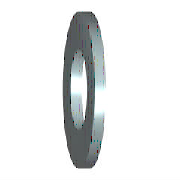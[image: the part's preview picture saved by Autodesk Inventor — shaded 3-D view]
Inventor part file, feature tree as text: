
AUTODESK INVENTOR PART (.ipt)
format: ipt  version: 2019.2 (Build 232265000, 265)  size: 106,496 bytes
history: native  units: mm (DEFAULTED — no unit token found)
features: other x1, plane x1, sketch x1
ambient origin geometry x7: Origin, YZ Plane, XY Plane, X Axis, Y Axis, Z Axis, Center Point
bodies: Solid1 (feature_tree), Body (feature_tree)
feature tree (3):
  other  "Work Axis1"
  plane  "Work Plane1"
  sketch  "Sketch"  dims[d0=10.5mm d1=18.0mm d2=1.6mm d3=0.0mm d4=0.0mm d5=0.0mm d6=0.0mm d7=0.0mm]
